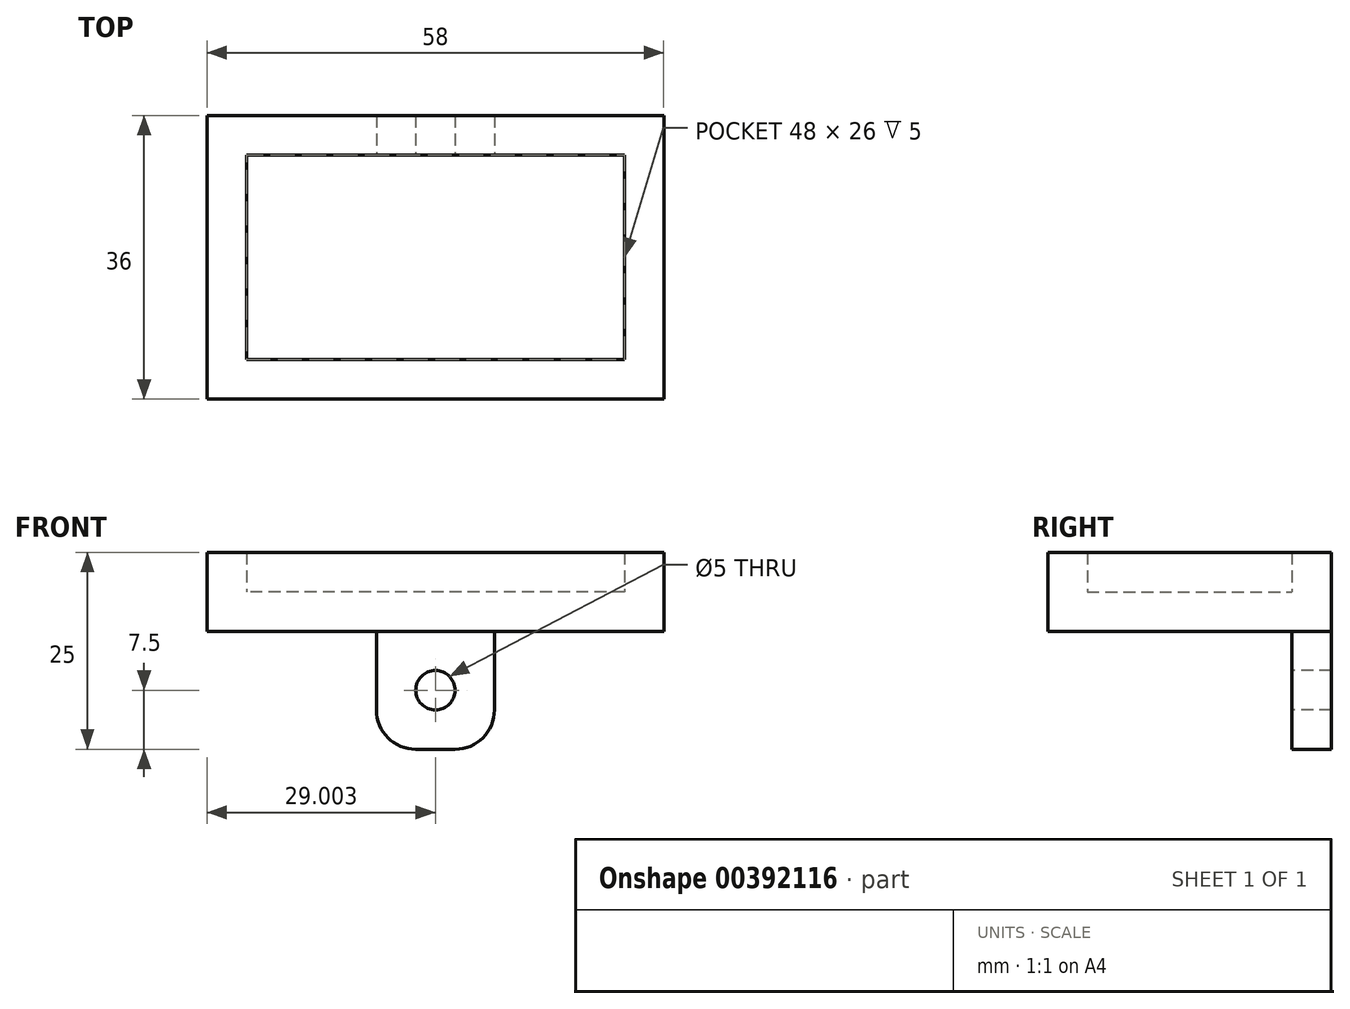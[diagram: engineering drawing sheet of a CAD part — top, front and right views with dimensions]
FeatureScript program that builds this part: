
annotation { "Feature Type Name" : "Feature", "Feature Type Description" : "" }
export const myFeature = defineFeature(function(context is Context, id is Id, definition is map)
    precondition{}
    {
        {
            var Q0;
            Q0=qCreatedBy(makeId("Top.planeOp"),FACE);
            var sketch = newSketch(context, id + "F0", { "sketchPlane" : qUnion([Q0])});
            skLineSegment(sketch, "E0.top", {"start": v(-22.68, 6.37) * mm, "end": v(25.32, 6.37) * mm});
            skLineSegment(sketch, "E0.left", {"start": v(-22.68, 32.37) * mm, "end": v(-22.68, 6.37) * mm});
            skLineSegment(sketch, "E0.right", {"start": v(25.32, 32.37) * mm, "end": v(25.32, 6.37) * mm});
            skPoint(sketch, "E1.startSnap0", {"position": v(-22.68, 19.37) * mm});
            skLineSegment(sketch, "E2", {"start": v(30.32, 37.37) * mm, "end": v(30.32, 1.37) * mm});
            skLineSegment(sketch, "E3", {"start": v(30.32, 1.37) * mm, "end": v(-27.68, 1.37) * mm});
            skLineSegment(sketch, "E4", {"start": v(-27.68, 1.37) * mm, "end": v(-27.68, 37.37) * mm});
            skPoint(sketch, "E1.start.orphan", {"position": v(-21.18, 19.37) * mm});
            skLineSegment(sketch, "E5", {"start": v(-22.68, 32.37) * mm, "end": v(25.32, 32.37) * mm});
            skPoint(sketch, "E6.start.orphan", {"position": v(-8.68, 37.37) * mm});
            skLineSegment(sketch, "E7", {"start": v(-27.68, 37.37) * mm, "end": v(30.32, 37.37) * mm});
            skSolve(sketch);
        }
        {
            var Q0;
            Q0 = qSketchRegion(id + "F0", true);
            var Q1;
            Q1=makeQuery(id+"F0.imprint","IMPRINT",FACE,{"disambiguationData":[TD([[makeQuery(id+"F0.imprint","IMPRINT",EDGE,{"derivedFrom":sQuery(id+"F0.wireOp",EDGE,"E0.top")}),1.0]])]});
            extrude(context, id + "F1", {"entities" : qUnion([Q0, Q1]), "depth" : 5 * mm});
        }
        {
            var Q0;
            Q0=makeQuery(id+"F0.imprint","IMPRINT",FACE,{"disambiguationData":[TD([[makeQuery(id+"F0.imprint","IMPRINT",EDGE,{"derivedFrom":sQuery(id+"F0.wireOp",EDGE,"E0.top")}),-1.0]])]});
            extrude(context, id + "F2", {"entities" : qUnion([Q0]), "operationType" : NewBodyOperationType.ADD, "depth" : 10 * mm});
        }
        {
            var Q0;
            Q0=makeQuery(id+"F1.opExtrude","CAP_FACE",FACE,{"disambiguationData":[OSD([sQuery(id+"F0.wireOp",EDGE,"E2"),sQuery(id+"F0.wireOp",EDGE,"E3"),sQuery(id+"F0.wireOp",EDGE,"E4"),sQuery(id+"F0.wireOp",EDGE,"E7")])],"isStart":true});
            var sketch = newSketch(context, id + "F3", { "sketchPlane" : qUnion([Q0])});
            skLineSegment(sketch, "E8.bottom", {"start": v(-6.18, -37.37) * mm, "end": v(8.82, -37.37) * mm});
            skLineSegment(sketch, "E8.top", {"start": v(-6.18, -32.37) * mm, "end": v(8.82, -32.37) * mm});
            skLineSegment(sketch, "E8.left", {"start": v(-6.18, -37.37) * mm, "end": v(-6.18, -32.37) * mm});
            skLineSegment(sketch, "E8.right", {"start": v(8.82, -37.37) * mm, "end": v(8.82, -32.37) * mm});
            skSolve(sketch);
        }
        {
            var Q0;
            Q0 = qSketchRegion(id + "F3", true);
            var Q1;
            Q1 = qSketchRegion(id + "FmQw1SfWzWPLqdI_1", true);
            extrude(context, id + "F4", {"entities" : qUnion([Q0, Q1]), "operationType" : NewBodyOperationType.ADD, "depth" : 15 * mm});
        }
        {
            var Q0;
            Q0=makeQuery(id+"F4.opExtrude","SWEPT_FACE",FACE,{"disambiguationData":[OSD([sQuery(id+"F3.wireOp",EDGE,"E8.top")])]});
            var sketch = newSketch(context, id + "F5", { "sketchPlane" : qUnion([Q0])});
            skCircle(sketch, "E9", {"center": v(1.32, -7.5) * mm, "radius": 2.5 * mm});
            skPoint(sketch, "E9.centerSnap0", {"position": v(-6.18, -7.5) * mm});
            skSolve(sketch);
        }
        {
            var Q0;
            Q0=makeQuery(id+"F5.imprint","IMPRINT",FACE,{"disambiguationData":[TD([[makeQuery(id+"F5.imprint","IMPRINT",EDGE,{"derivedFrom":sQuery(id+"F5.wireOp",EDGE,"E9")}),1.0]])]});
            var Q1;
            Q1=sQuery(id+"F5.wireOp",EDGE,"E9");
            extrude(context, id + "F6", {"entities" : qUnion([Q0]), "operationType" : NewBodyOperationType.REMOVE, "surfaceEntities" : qUnion([Q1]), "oppositeDirection" : true, "depth" : 25 * mm});
        }
        {
            var Q0;
            Q0=makeQuery(id+"F4.opExtrude","CAP_EDGE",EDGE,{"disambiguationData":[OSD([sQuery(id+"F3.wireOp",EDGE,"E8.right")])],"isStart":false});
            var Q1;
            Q1=makeQuery(id+"F4.opExtrude","CAP_EDGE",EDGE,{"disambiguationData":[OSD([sQuery(id+"F3.wireOp",EDGE,"E8.left")])],"isStart":false});
            var Q2;
            Q2=makeQuery(id+"F4.opExtrude","CAP_EDGE",EDGE,{"disambiguationData":[OSD([sQuery(id+"F3.wireOp",EDGE,"E8.right")])],"isStart":true});
            var Q3;
            Q3=makeQuery(id+"F4.opExtrude","CAP_EDGE",EDGE,{"disambiguationData":[OSD([sQuery(id+"F3.wireOp",EDGE,"E8.left")])],"isStart":true});
            fillet(context, id + "F7", {"entities" : qUnion([Q0, Q1, Q2, Q3]), "radius" : 5 * mm, "tangentPropagation" : true, "allowEdgeOverflow" : false});
        }
    });
